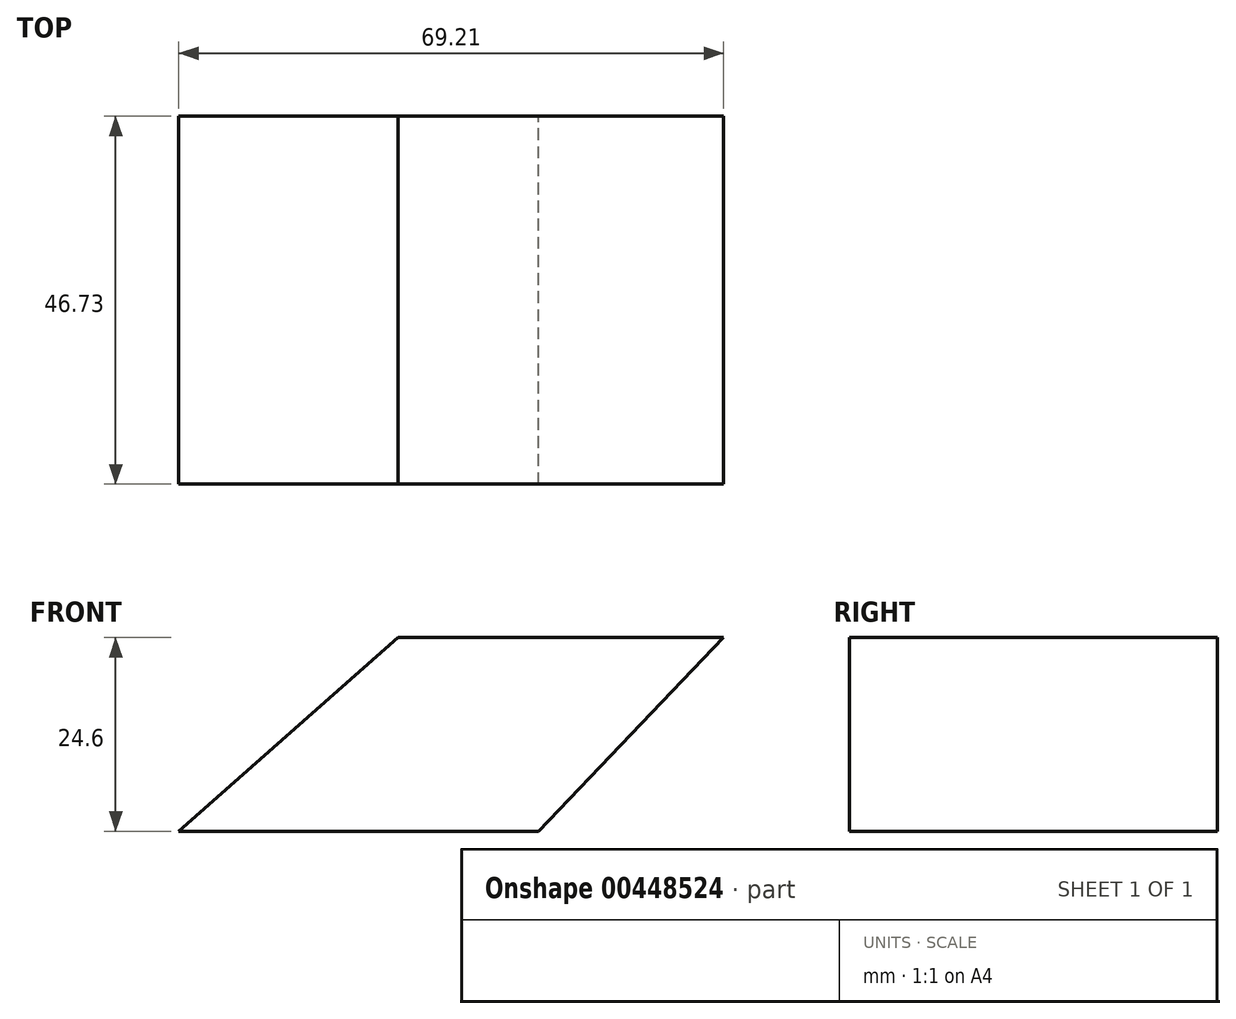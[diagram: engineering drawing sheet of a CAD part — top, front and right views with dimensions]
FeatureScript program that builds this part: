
annotation { "Feature Type Name" : "Feature", "Feature Type Description" : "" }
export const myFeature = defineFeature(function(context is Context, id is Id, definition is map)
    precondition{}
    {
        {
            var Q0;
            Q0=qCreatedBy(makeId("Front.planeOp"),FACE);
            var sketch = newSketch(context, id + "F0", { "sketchPlane" : qUnion([Q0])});
            skLineSegment(sketch, "E0", {"start": v(-27.84, -16.19) * mm, "end": v(17.84, -16.19) * mm});
            skLineSegment(sketch, "E1", {"start": v(17.84, -16.19) * mm, "end": v(41.37, 8.4) * mm});
            skLineSegment(sketch, "E2", {"start": v(41.37, 8.4) * mm, "end": v(0, 8.4) * mm});
            skLineSegment(sketch, "E3", {"start": v(0, 8.4) * mm, "end": v(-27.84, -16.19) * mm});
            skSolve(sketch);
        }
        {
            var Q0;
            Q0 = qSketchRegion(id + "F0", true);
            extrude(context, id + "F1", {"entities" : qUnion([Q0]), "depth" : 46.73 * mm});
        }
    });
